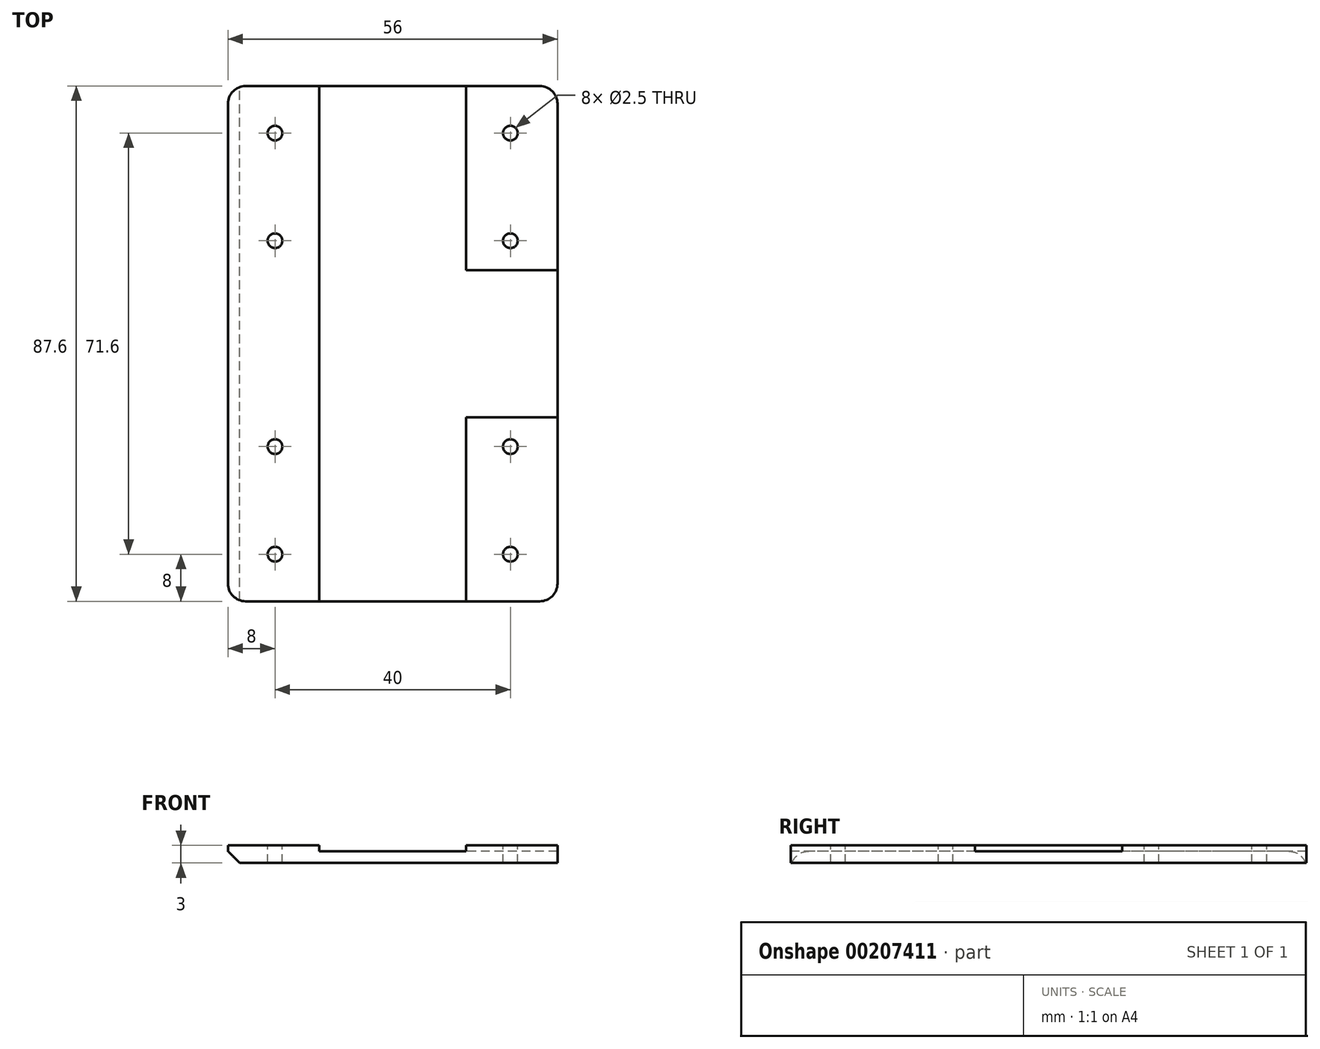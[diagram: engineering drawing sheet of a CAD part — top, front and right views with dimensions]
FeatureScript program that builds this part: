
annotation { "Feature Type Name" : "Feature", "Feature Type Description" : "" }
export const myFeature = defineFeature(function(context is Context, id is Id, definition is map)
    precondition{}
    {
        {
            var Q0;
            Q0=qCreatedBy(makeId("Top.planeOp"),FACE);
            var sketch = newSketch(context, id + "F0", { "sketchPlane" : qUnion([Q0])});
            skLineSegment(sketch, "E0.bottom", {"start": v(28, -43.8) * mm, "end": v(-28, -43.8) * mm});
            skLineSegment(sketch, "E0.top", {"start": v(28, 43.8) * mm, "end": v(-28, 43.8) * mm});
            skLineSegment(sketch, "E0.left", {"start": v(28, -43.8) * mm, "end": v(28, 43.8) * mm});
            skLineSegment(sketch, "E0.right", {"start": v(-28, -43.8) * mm, "end": v(-28, 43.8) * mm});
            skPoint(sketch, "E0.middle", {"position": v(0, 0) * mm});
            skSolve(sketch);
        }
        {
            var Q0;
            Q0=makeQuery(id+"F0.imprint","IMPRINT",FACE,{"disambiguationData":[TD([[makeQuery(id+"F0.imprint","IMPRINT",EDGE,{"derivedFrom":sQuery(id+"F0.wireOp",EDGE,"E0.bottom")}),-1.0]])]});
            extrude(context, id + "F1", {"entities" : qUnion([Q0]), "depth" : 3 * mm});
        }
        {
            var Q0;
            Q0=makeQuery(id+"F1.opExtrude","CAP_FACE",FACE,{"disambiguationData":[OSD([sQuery(id+"F0.wireOp",EDGE,"E0.bottom"),sQuery(id+"F0.wireOp",EDGE,"E0.top"),sQuery(id+"F0.wireOp",EDGE,"E0.left"),sQuery(id+"F0.wireOp",EDGE,"E0.right")])],"isStart":false});
            var sketch = newSketch(context, id + "F9", { "sketchPlane" : qUnion([Q0])});
            skCircle(sketch, "E1", {"center": v(28, 28.8) * mm, "radius": 10 * mm});
            skSolve(sketch);
        }
        {
            var Q0;
            Q0=makeQuery(id+"F1.opExtrude","CAP_EDGE",EDGE,{"disambiguationData":[OSD([sQuery(id+"F0.wireOp",EDGE,"E0.right")])],"isStart":true});
            chamfer(context, id + "F2", {"entities" : qUnion([Q0]), "width" : 2 * mm, "tangentPropagation" : true});
        }
        {
            var Q0;
            Q0=makeQuery(id+"F1.opExtrude","CAP_FACE",FACE,{"disambiguationData":[OSD([sQuery(id+"F0.wireOp",EDGE,"E0.bottom"),sQuery(id+"F0.wireOp",EDGE,"E0.top"),sQuery(id+"F0.wireOp",EDGE,"E0.left"),sQuery(id+"F0.wireOp",EDGE,"E0.right")])],"isStart":false});
            var sketch = newSketch(context, id + "F3", { "sketchPlane" : qUnion([Q0])});
            skLineSegment(sketch, "E2", {"start": v(-12.5, 43.8) * mm, "end": v(-12.5, -43.8) * mm});
            skLineSegment(sketch, "E3", {"start": v(12.5, 43.8) * mm, "end": v(12.5, -43.8) * mm});
            skLineSegment(sketch, "E4", {"start": v(-12.5, 43.8) * mm, "end": v(12.5, 43.8) * mm});
            skLineSegment(sketch, "E5", {"start": v(12.5, -43.8) * mm, "end": v(-12.5, -43.8) * mm});
            skLineSegment(sketch, "E6", {"start": v(12.5, 12.5) * mm, "end": v(28, 12.5) * mm});
            skLineSegment(sketch, "E7", {"start": v(28, 12.5) * mm, "end": v(28, -12.5) * mm});
            skLineSegment(sketch, "E8", {"start": v(28, -12.5) * mm, "end": v(12.5, -12.5) * mm});
            skPoint(sketch, "E9", {"position": v(0, 43.8) * mm});
            skPoint(sketch, "E10", {"position": v(28, 0) * mm});
            skSolve(sketch);
        }
        {
            var Q0;
            Q0=makeQuery(id+"F3.imprint","IMPRINT",FACE,{"disambiguationData":[TD([[makeQuery(id+"F3.imprint","IMPRINT",EDGE,{"derivedFrom":sQuery(id+"F3.wireOp",EDGE,"E2")}),1.0]])]});
            var Q1;
            {var subQ0=sQuery(id+"F3.wireOp",EDGE,"E6");Q1=makeQuery(id+"F3.imprint","IMPRINT",FACE,{"disambiguationData":[TD([[makeQuery(id+"F3.imprint","IMPRINT",EDGE,{"derivedFrom":subQ0}),-1.0]])]});}
            extrude(context, id + "F4", {"entities" : qUnion([Q0, Q1]), "operationType" : NewBodyOperationType.REMOVE, "oppositeDirection" : true, "depth" : 1 * mm});
        }
        {
            var Q0;
            Q0=makeQuery(id+"F1.opExtrude","SWEPT_EDGE",EDGE,{"disambiguationData":[OSD([sQuery(id+"F0.wireOp",EDGE,"E0.top"),sQuery(id+"F0.wireOp",EDGE,"E0.right")])]});
            var Q1;
            Q1=makeQuery(id+"F1.opExtrude","SWEPT_EDGE",EDGE,{"disambiguationData":[OSD([sQuery(id+"F0.wireOp",EDGE,"E0.bottom"),sQuery(id+"F0.wireOp",EDGE,"E0.right")])]});
            var Q2;
            Q2=makeQuery(id+"F1.opExtrude","SWEPT_EDGE",EDGE,{"disambiguationData":[OSD([sQuery(id+"F0.wireOp",EDGE,"E0.bottom"),sQuery(id+"F0.wireOp",EDGE,"E0.left")])]});
            var Q3;
            Q3=makeQuery(id+"F1.opExtrude","SWEPT_EDGE",EDGE,{"disambiguationData":[OSD([sQuery(id+"F0.wireOp",EDGE,"E0.top"),sQuery(id+"F0.wireOp",EDGE,"E0.left")])]});
            fillet(context, id + "F5", {"entities" : qUnion([Q0, Q1, Q2, Q3]), "radius" : 3 * mm, "tangentPropagation" : true, "allowEdgeOverflow" : false});
        }
        {
            var Q0;
            {var subQ0=sQuery(id+"F0.wireOp",EDGE,"E0.bottom");var subQ1=sQuery(id+"F0.wireOp",EDGE,"E0.top");var subQ2=sQuery(id+"F0.wireOp",EDGE,"E0.right");Q0=makeQuery(id+"F4.boolean.opBoolean","SPLIT",FACE,{"disambiguationData":[TD([makeQuery(id+"F1.opExtrude","SWEPT_FACE",FACE,{"disambiguationData":[OSD([subQ2])]})])],"derivedFrom":makeQuery(id+"F1.opExtrude","CAP_FACE",FACE,{"disambiguationData":[OSD([subQ0,subQ1,sQuery(id+"F0.wireOp",EDGE,"E0.left"),subQ2])],"isStart":false})});}
            cPlane(context, id + "F6", {"entities" : qUnion([Q0]), "cplaneType" : CPlaneType.OFFSET, "offset" : 0 * mm, "width" : 150 * mm, "height" : 150 * mm});
        }
        {
            var Q0;
            Q0=qCreatedBy(id+"F6.planeOp",FACE);
            var sketch = newSketch(context, id + "F7", { "sketchPlane" : qUnion([Q0])});
            skLineSegment(sketch, "E11.0", {"start": v(-12.5, 43.8) * mm, "end": v(-25, 43.8) * mm, "construction": true});
            skLineSegment(sketch, "E12.0", {"start": v(-28, -40.8) * mm, "end": v(-28, 40.8) * mm, "construction": true});
            skLineSegment(sketch, "E13.0", {"start": v(25, 43.8) * mm, "end": v(12.5, 43.8) * mm, "construction": true});
            skLineSegment(sketch, "E14.0", {"start": v(28, 12.5) * mm, "end": v(28, 40.8) * mm, "construction": true});
            skPoint(sketch, "E15.0", {"position": v(18.75, -43.8) * mm});
            skLineSegment(sketch, "E16.0", {"start": v(25, -43.8) * mm, "end": v(12.5, -43.8) * mm});
            skLineSegment(sketch, "E17.0", {"start": v(28, -40.8) * mm, "end": v(28, -12.5) * mm});
            skLineSegment(sketch, "E18.bottom", {"start": v(-25, 40.8) * mm, "end": v(25, 40.8) * mm});
            skLineSegment(sketch, "E18.top", {"start": v(-25, -40.8) * mm, "end": v(25, -40.8) * mm});
            skLineSegment(sketch, "E18.left", {"start": v(-25, 40.8) * mm, "end": v(-25, -40.8) * mm});
            skLineSegment(sketch, "E18.right", {"start": v(25, 40.8) * mm, "end": v(25, -40.8) * mm});
            skPoint(sketch, "E19", {"position": v(-20, -35.8) * mm});
            skPoint(sketch, "E20", {"position": v(20, -35.8) * mm});
            skPoint(sketch, "E21", {"position": v(20, -17.5) * mm});
            skPoint(sketch, "E22", {"position": v(20, 17.5) * mm});
            skPoint(sketch, "E23", {"position": v(20, 35.8) * mm});
            skPoint(sketch, "E24", {"position": v(-20, 35.8) * mm});
            skPoint(sketch, "E25", {"position": v(-20, 17.5) * mm});
            skPoint(sketch, "E26", {"position": v(-20, -17.5) * mm});
            skSolve(sketch);
        }
        {
            var Q0;
            Q0=sQuery(id+"F7.wireOp",VERTEX,"E24");
            var Q1;
            Q1=sQuery(id+"F7.wireOp",VERTEX,"E23");
            var Q2;
            Q2=sQuery(id+"F7.wireOp",VERTEX,"E22");
            var Q3;
            Q3=sQuery(id+"F7.wireOp",VERTEX,"E21");
            var Q4;
            Q4=sQuery(id+"F7.wireOp",VERTEX,"E20");
            var Q5;
            Q5=sQuery(id+"F7.wireOp",VERTEX,"E19");
            var Q6;
            Q6=sQuery(id+"F7.wireOp",VERTEX,"E25");
            var Q7;
            Q7=sQuery(id+"F7.wireOp",VERTEX,"E26");
            var Q8;
            Q8=makeQuery(id+"F1.opExtrude","SWEPT_BODY",BODY,{"disambiguationData":[OSD([sQuery(id+"F0.wireOp",EDGE,"E0.bottom"),sQuery(id+"F0.wireOp",EDGE,"E0.top"),sQuery(id+"F0.wireOp",EDGE,"E0.left"),sQuery(id+"F0.wireOp",EDGE,"E0.right")])]});
            hole(context, id + "F8", {"style" : HoleStyle.SIMPLE, "endStyle" : HoleEndStyle.BLIND, "holeDiameter" : 2.5 * mm, "holeDepth" : 68 * mm, "locations" : qUnion([Q0, Q1, Q2, Q3, Q4, Q5, Q6, Q7]), "scope" : qUnion([Q8])});
        }
    });
